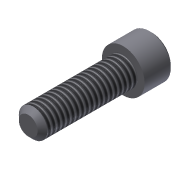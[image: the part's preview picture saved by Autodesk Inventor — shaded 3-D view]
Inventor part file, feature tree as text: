
AUTODESK INVENTOR PART (.ipt)
format: ipt  version: 2013 (Build 170138000, 138)  size: 109,568 bytes
history: native  units: in
note: dims shown in document units (in); Inventor stores cm internally (conversion verified against a paired STEP export)
features: extrude x3, sketch x3, chamfer x2, thread x1
ambient origin geometry x8: Origin, YZ Plane, XZ Plane, XY Plane, X Axis, Y Axis, Z Axis, Center Point
bodies: Solid1 (feature_tree)
feature tree (9):
  extrude  "Extrusion1"  Depth=0.3937in TaperAngle=0.0deg
  extrude  "Extrusion2"  Depth=0.1181in TaperAngle=0.0deg
  extrude  "Extrusion3"  Depth=0.0591in TaperAngle=0.0deg
  thread  "Thread1"  [1 undecoded]
  chamfer  "Chamfer1"  [1 undecoded]
  chamfer  "Chamfer2"  [1 undecoded]
  sketch  "Sketch1"  dims[d0=0.1181in d1=0.3937in d2=0.0in]
  sketch  "Sketch2"  dims[d3=0.1772in d4=0.1181in d5=0.0in]
  sketch  "Sketch3"  dims[d6=0.0984in d7=0.0591in d8=0.0in d9=0.8661in d10=0.0in d11=0.02in d12=0.125in d13=45.0deg d15=0.0098in d16=0.0787in d17=45.0deg]
note: 3 required parameter values undecoded (feature->parameter linkage not recoverable at this tier; creation-order binding heuristic only, values carry confidence <= 0.55)
